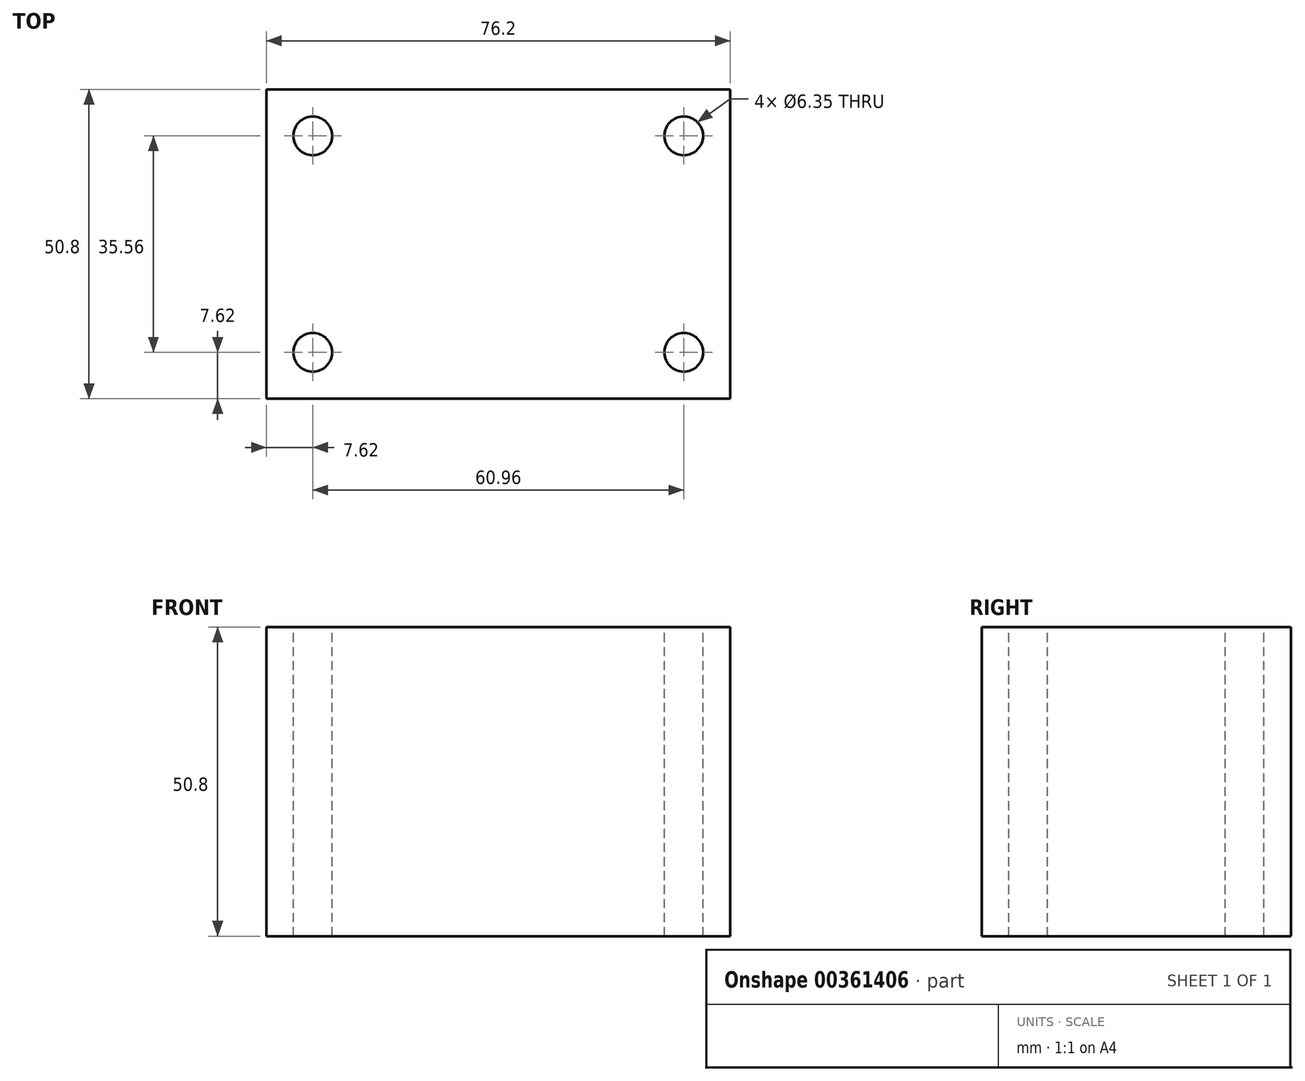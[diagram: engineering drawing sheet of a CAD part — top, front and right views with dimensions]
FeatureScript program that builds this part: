
annotation { "Feature Type Name" : "Feature", "Feature Type Description" : "" }
export const myFeature = defineFeature(function(context is Context, id is Id, definition is map)
    precondition{}
    {
        {
            var Q0;
            Q0=qCreatedBy(makeId("Front.planeOp"),FACE);
            var sketch = newSketch(context, id + "F0", { "sketchPlane" : qUnion([Q0])});
            skLineSegment(sketch, "E0.bottom", {"start": v(38.1, 25.4) * mm, "end": v(-38.1, 25.4) * mm});
            skLineSegment(sketch, "E0.top", {"start": v(38.1, -25.4) * mm, "end": v(-38.1, -25.4) * mm});
            skLineSegment(sketch, "E0.left", {"start": v(38.1, 25.4) * mm, "end": v(38.1, -25.4) * mm});
            skLineSegment(sketch, "E0.right", {"start": v(-38.1, 25.4) * mm, "end": v(-38.1, -25.4) * mm});
            skPoint(sketch, "E0.middle", {"position": v(0, 0) * mm});
            skSolve(sketch);
        }
        {
            var Q0;
            Q0=makeQuery(id+"F0.imprint","IMPRINT",FACE,{"disambiguationData":[TD([[makeQuery(id+"F0.imprint","IMPRINT",EDGE,{"derivedFrom":sQuery(id+"F0.wireOp",EDGE,"E0.bottom")}),1.0]])]});
            extrude(context, id + "F1", {"entities" : qUnion([Q0]), "endBound" : BoundingType.SYMMETRIC, "depth" : 50.8 * mm});
        }
        {
            var Q0;
            Q0=makeQuery(id+"F1.opExtrude","SWEPT_FACE",FACE,{"disambiguationData":[OSD([sQuery(id+"F0.wireOp",EDGE,"E0.bottom")])]});
            var sketch = newSketch(context, id + "F2", { "sketchPlane" : qUnion([Q0])});
            skCircle(sketch, "E1", {"center": v(30.48, -17.78) * mm, "radius": 3.81 * mm});
            skCircle(sketch, "E2.MirrorC", {"center": v(-30.48, -17.78) * mm, "radius": 3.81 * mm});
            skCircle(sketch, "E3.MirrorC", {"center": v(30.48, 17.78) * mm, "radius": 3.81 * mm});
            skCircle(sketch, "E4.MirrorC", {"center": v(-30.48, 17.78) * mm, "radius": 3.81 * mm});
            skLineSegment(sketch, "E5.bottom", {"start": v(-12.7, 25.4) * mm, "end": v(12.7, 25.4) * mm});
            skLineSegment(sketch, "E5.top", {"start": v(-12.7, 19.05) * mm, "end": v(12.7, 19.05) * mm});
            skLineSegment(sketch, "E5.left", {"start": v(-12.7, 25.4) * mm, "end": v(-12.7, 19.05) * mm});
            skLineSegment(sketch, "E5.right", {"start": v(12.7, 25.4) * mm, "end": v(12.7, 19.05) * mm});
            skSolve(sketch);
        }
        {
            var Q0;
            Q0=sQuery(id+"F2.wireOp",VERTEX,"E1.center");
            var Q1;
            Q1=sQuery(id+"F2.wireOp",VERTEX,"E2.MirrorC.center");
            var Q2;
            Q2=sQuery(id+"F2.wireOp",VERTEX,"E3.MirrorC.center");
            var Q3;
            Q3=sQuery(id+"F2.wireOp",VERTEX,"E4.MirrorC.center");
            var Q4;
            Q4=makeQuery(id+"F1.opExtrude","SWEPT_BODY",BODY,{"disambiguationData":[OSD([sQuery(id+"F0.wireOp",EDGE,"E0.bottom"),sQuery(id+"F0.wireOp",EDGE,"E0.top"),sQuery(id+"F0.wireOp",EDGE,"E0.left"),sQuery(id+"F0.wireOp",EDGE,"E0.right")])]});
            hole(context, id + "F3", {"style" : HoleStyle.SIMPLE, "endStyle" : HoleEndStyle.THROUGH, "holeDiameter" : 6.35 * mm, "isTappedThrough" : true, "tappedDepth" : 12.7 * mm, "tapClearance" : 3, "locations" : qUnion([Q0, Q1, Q2, Q3]), "scope" : qUnion([Q4])});
        }
    });
